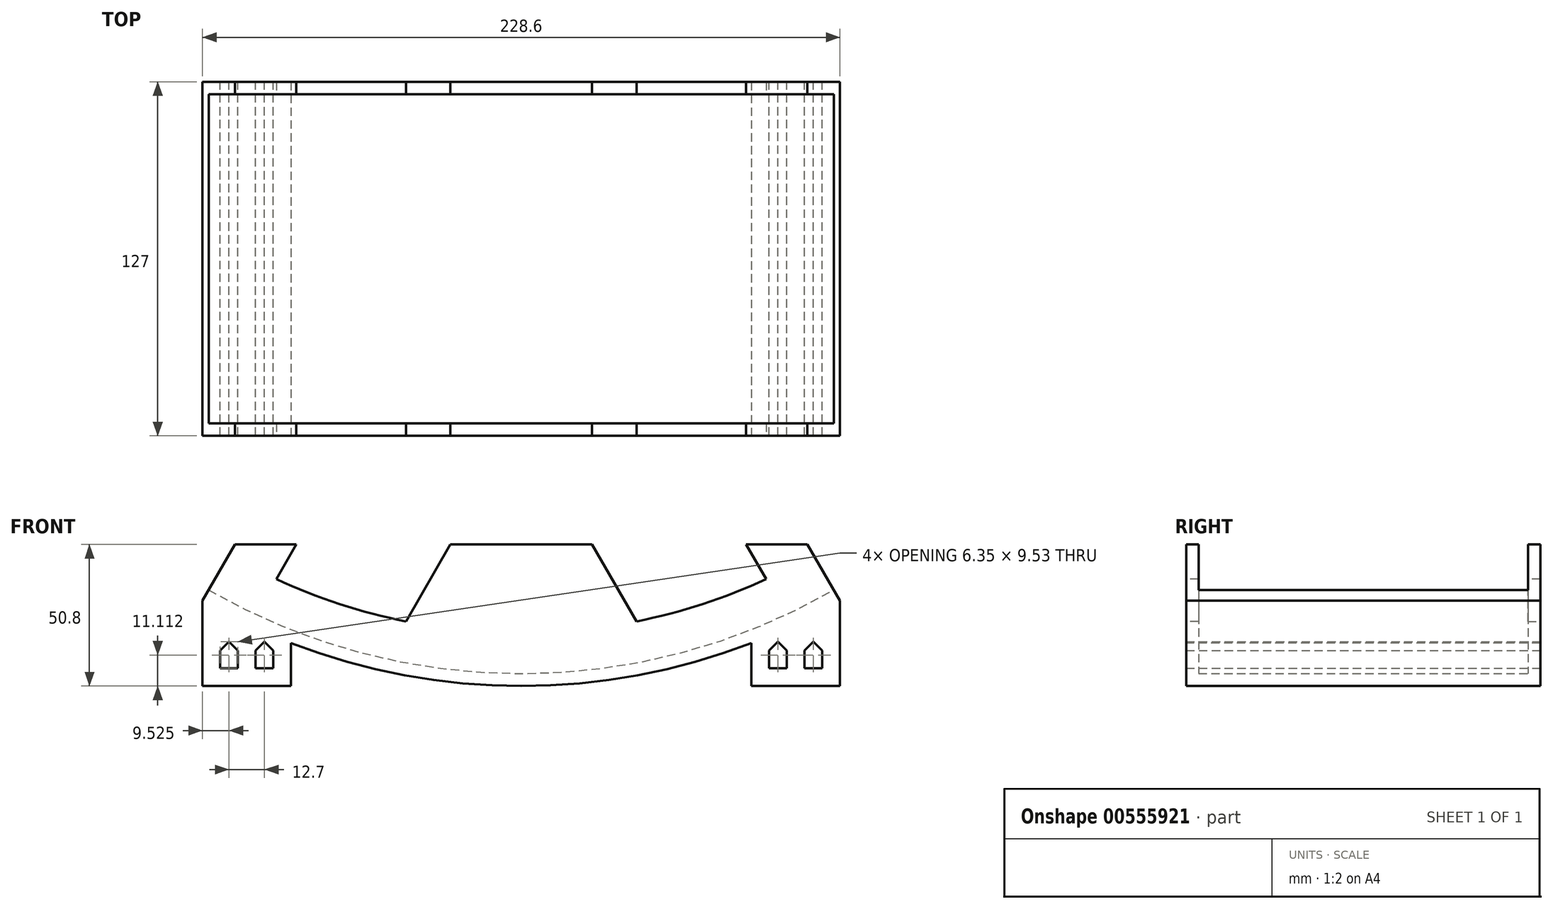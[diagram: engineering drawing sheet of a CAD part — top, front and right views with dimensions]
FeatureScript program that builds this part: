
annotation { "Feature Type Name" : "Feature", "Feature Type Description" : "" }
export const myFeature = defineFeature(function(context is Context, id is Id, definition is map)
    precondition{}
    {
        {
            var Q0;
            Q0=qCreatedBy(makeId("Front.planeOp"),FACE);
            var sketch = newSketch(context, id + "F0", { "sketchPlane" : qUnion([Q0])});
            skArc(sketch, "E0", {"start": v(-228.6, 0) * mm, "mid": v(0, -228.6) * mm, "end": v(228.6, 0) * mm});
            skLineSegment(sketch, "E1", {"start": v(-38.1, 0) * mm, "end": v(-228.6, 0) * mm});
            skLineSegment(sketch, "E2", {"start": v(38.1, 0) * mm, "end": v(228.6, 0) * mm});
            skLineSegment(sketch, "E3", {"start": v(-19.05, -33) * mm, "end": v(-114.3, -197.97) * mm});
            skLineSegment(sketch, "E4", {"start": v(19.05, -33) * mm, "end": v(114.3, -197.97) * mm});
            skArc(sketch, "E5", {"start": v(19.05, -33) * mm, "mid": v(0, 38.1) * mm, "end": v(-19.05, -33) * mm});
            skSolve(sketch);
        }
        {
            var Q0;
            {var subQ3=sQuery(id+"F0.wireOp",EDGE,"E3");Q0=makeQuery(id+"F0.imprint","IMPRINT",FACE,{"disambiguationData":[TD([[makeQuery(id+"F0.imprint","IMPRINT",EDGE,{"derivedFrom":subQ3}),1.0]])]});}
            extrude(context, id + "F1", {"entities" : qUnion([Q0]), "depth" : 127 * mm, "offsetDistance" : 25.4 * mm});
        }
        {
            var Q0;
            Q0=makeQuery(id+"F1.opExtrude","SWEPT_FACE",FACE,{"disambiguationData":[OSD([sQuery(id+"F0.wireOp",EDGE,"E5")])]});
            var Q1;
            Q1=makeQuery(id+"F1.opExtrude","SWEPT_FACE",FACE,{"disambiguationData":[OSD([sQuery(id+"F0.wireOp",EDGE,"E4")])]});
            var Q2;
            Q2=makeQuery(id+"F1.opExtrude","SWEPT_FACE",FACE,{"disambiguationData":[OSD([sQuery(id+"F0.wireOp",EDGE,"E3")])]});
            shell(context, id + "F2", {"entities" : qUnion([Q0, Q1, Q2]), "thickness" : 4.44 * mm});
        }
        {
            var Q0;
            Q0=makeQuery(id+"F1.opExtrude","CAP_FACE",FACE,{"disambiguationData":[OSD([sQuery(id+"F0.wireOp",EDGE,"E0"),sQuery(id+"F0.wireOp",EDGE,"E3"),sQuery(id+"F0.wireOp",EDGE,"E4"),sQuery(id+"F0.wireOp",EDGE,"E5")])],"isStart":false});
            var sketch = newSketch(context, id + "F3", { "sketchPlane" : qUnion([Q0])});
            skLineSegment(sketch, "E6.0", {"start": v(7.05, -50.3) * mm, "end": v(87.84, -190.25) * mm});
            skArc(sketch, "E6.1", {"start": v(-87.84, -190.25) * mm, "mid": v(-48.4, -203.88) * mm, "end": v(-7.05, -209.43) * mm});
            skCircle(sketch, "E7", {"center": v(0, 0) * mm, "radius": 9.53 * mm});
            skLineSegment(sketch, "E8", {"start": v(-7.05, -50.3) * mm, "end": v(-7.05, -125.9) * mm});
            skLineSegment(sketch, "E9", {"start": v(7.05, -50.3) * mm, "end": v(7.05, -125.9) * mm});
            skLineSegment(sketch, "E10", {"start": v(-87.84, -190.25) * mm, "end": v(-50.62, -125.78) * mm});
            skPoint(sketch, "E11.endSnap0", {"position": v(-66.67, -115.48) * mm});
            skLineSegment(sketch, "E12", {"start": v(-44.27, -114.78) * mm, "end": v(-14.9, -131.73) * mm});
            skLineSegment(sketch, "E13.trimOffspring", {"start": v(-7.05, -169.35) * mm, "end": v(-7.05, -209.43) * mm});
            skLineSegment(sketch, "E14.trimOffspring", {"start": v(-50.62, -125.78) * mm, "end": v(-87.84, -190.25) * mm});
            skArc(sketch, "E15.trimOffspring", {"start": v(7.05, -209.43) * mm, "mid": v(48.4, -203.88) * mm, "end": v(87.84, -190.25) * mm});
            skLineSegment(sketch, "E16", {"start": v(-7.05, -50.3) * mm, "end": v(0, -50.3) * mm, "construction": true});
            skLineSegment(sketch, "E17", {"start": v(0, -50.3) * mm, "end": v(0, -85.39) * mm, "construction": true});
            skLineSegment(sketch, "E18", {"start": v(-44.27, -114.78) * mm, "end": v(-7.05, -50.3) * mm});
            skLineSegment(sketch, "E19.MirrorCS", {"start": v(44.27, -114.78) * mm, "end": v(14.9, -131.73) * mm});
            skLineSegment(sketch, "E20.trimOffspring", {"start": v(7.05, -169.35) * mm, "end": v(7.05, -209.43) * mm});
            skArc(sketch, "E21", {"start": v(14.9, -131.73) * mm, "mid": v(11.36, -128.3) * mm, "end": v(7.05, -125.9) * mm});
            skPoint(sketch, "E22.orphan", {"position": v(7.05, -136.27) * mm});
            skPoint(sketch, "E23.orphan", {"position": v(7.05, -150.93) * mm});
            skPoint(sketch, "E24.orphan", {"position": v(-7.05, -150.93) * mm});
            skPoint(sketch, "E25.orphan", {"position": v(-7.05, -136.27) * mm});
            skLineSegment(sketch, "E26", {"start": v(50.62, -125.78) * mm, "end": v(7.05, -169.35) * mm, "construction": true});
            skLineSegment(sketch, "E27", {"start": v(50.62, -125.78) * mm, "end": v(7.05, -169.35) * mm});
            skLineSegment(sketch, "E28.MirrorCS", {"start": v(-50.62, -125.78) * mm, "end": v(-7.05, -169.35) * mm});
            skArc(sketch, "E29.trimOffspring", {"start": v(-7.05, -125.9) * mm, "mid": v(-11.36, -128.3) * mm, "end": v(-14.9, -131.73) * mm});
            skSolve(sketch);
        }
        {
            var Q0;
            Q0=makeQuery(id+"F3.imprint","IMPRINT",FACE,{"disambiguationData":[TD([[makeQuery(id+"F3.imprint","IMPRINT",EDGE,{"derivedFrom":sQuery(id+"F3.wireOp",EDGE,"E6.1")}),1.0]])]});
            var Q1;
            {var subQ2=sQuery(id+"F3.wireOp",EDGE,"E15.trimOffspring");Q1=makeQuery(id+"F3.imprint","IMPRINT",FACE,{"disambiguationData":[TD([[makeQuery(id+"F3.imprint","IMPRINT",EDGE,{"derivedFrom":subQ2}),1.0]])]});}
            var Q2;
            {var subQ0=sQuery(id+"F3.wireOp",EDGE,"E9");Q2=makeQuery(id+"F3.imprint","IMPRINT",FACE,{"disambiguationData":[TD([[makeQuery(id+"F3.imprint","IMPRINT",EDGE,{"derivedFrom":subQ0}),1.0]])]});}
            var Q3;
            {var subQ0=sQuery(id+"F3.wireOp",EDGE,"E8");Q3=makeQuery(id+"F3.imprint","IMPRINT",FACE,{"disambiguationData":[TD([[makeQuery(id+"F3.imprint","IMPRINT",EDGE,{"derivedFrom":subQ0}),-1.0]])]});}
            var Q4;
            Q4=makeQuery(id+"F3.imprint","IMPRINT",FACE,{"disambiguationData":[TD([[makeQuery(id+"F3.imprint","IMPRINT",EDGE,{"derivedFrom":sQuery(id+"F3.wireOp",EDGE,"E7")}),1.0]])]});
            var Q5;
            Q5=makeQuery(id+"F1.opExtrude","CAP_FACE",FACE,{"disambiguationData":[OSD([sQuery(id+"F0.wireOp",EDGE,"E0"),sQuery(id+"F0.wireOp",EDGE,"E3"),sQuery(id+"F0.wireOp",EDGE,"E4"),sQuery(id+"F0.wireOp",EDGE,"E5")])],"isStart":true});
            extrude(context, id + "F4", {"entities" : qUnion([Q0, Q1, Q2, Q3, Q4]), "operationType" : NewBodyOperationType.REMOVE, "endBound" : BoundingType.UP_TO_SURFACE, "oppositeDirection" : true, "depth" : 25.4 * mm, "endBoundEntityFace" : qUnion([Q5]), "offsetDistance" : 25.4 * mm});
        }
        {
            var Q0;
            Q0=qCreatedBy(makeId("Front.planeOp"),FACE);
            var sketch = newSketch(context, id + "F5", { "sketchPlane" : qUnion([Q0])});
            skLineSegment(sketch, "E30", {"start": v(0, -228.6) * mm, "end": v(114.3, -228.6) * mm});
            skLineSegment(sketch, "E31", {"start": v(0, -228.6) * mm, "end": v(-114.3, -228.6) * mm});
            skLineSegment(sketch, "E32", {"start": v(114.3, -197.97) * mm, "end": v(114.3, -228.6) * mm});
            skLineSegment(sketch, "E33", {"start": v(-114.3, -197.97) * mm, "end": v(-114.3, -228.6) * mm});
            skPoint(sketch, "E34.orphan", {"position": v(-122.47, -228.6) * mm});
            skArc(sketch, "E35.0", {"start": v(-114.3, -197.97) * mm, "mid": v(0, -228.6) * mm, "end": v(114.3, -197.97) * mm});
            skLineSegment(sketch, "E36", {"start": v(114.3, -228.6) * mm, "end": v(107.95, -228.6) * mm, "construction": true});
            skLineSegment(sketch, "E37", {"start": v(107.95, -228.6) * mm, "end": v(107.95, -222.25) * mm, "construction": true});
            skLineSegment(sketch, "E38.bottom", {"start": v(107.95, -222.25) * mm, "end": v(101.6, -222.25) * mm});
            skLineSegment(sketch, "E38.left", {"start": v(107.95, -222.25) * mm, "end": v(107.95, -215.9) * mm});
            skLineSegment(sketch, "E38.right", {"start": v(88.9, -222.25) * mm, "end": v(88.9, -215.9) * mm});
            skLineSegment(sketch, "E39", {"start": v(101.6, -222.25) * mm, "end": v(101.6, -215.9) * mm});
            skLineSegment(sketch, "E40", {"start": v(95.25, -222.25) * mm, "end": v(95.25, -215.9) * mm});
            skLineSegment(sketch, "E41.trimOffspring", {"start": v(95.25, -222.25) * mm, "end": v(88.9, -222.25) * mm});
            skLineSegment(sketch, "E42", {"start": v(104.78, -215.9) * mm, "end": v(104.78, -212.72) * mm, "construction": true});
            skLineSegment(sketch, "E43", {"start": v(92.08, -215.9) * mm, "end": v(92.08, -212.72) * mm, "construction": true});
            skLineSegment(sketch, "E44", {"start": v(107.95, -215.9) * mm, "end": v(104.78, -212.72) * mm});
            skLineSegment(sketch, "E45", {"start": v(101.6, -215.9) * mm, "end": v(104.78, -212.72) * mm});
            skLineSegment(sketch, "E46", {"start": v(95.25, -215.9) * mm, "end": v(92.08, -212.72) * mm});
            skLineSegment(sketch, "E47", {"start": v(88.9, -215.9) * mm, "end": v(92.08, -212.72) * mm});
            skLineSegment(sketch, "E48.MirrorCS", {"start": v(-104.78, -215.9) * mm, "end": v(-104.78, -212.72) * mm, "construction": true});
            skLineSegment(sketch, "E49.MirrorCS", {"start": v(-92.08, -215.9) * mm, "end": v(-92.08, -212.72) * mm, "construction": true});
            skLineSegment(sketch, "E50.MirrorCS", {"start": v(-101.6, -215.9) * mm, "end": v(-104.78, -212.72) * mm});
            skLineSegment(sketch, "E51.MirrorCS", {"start": v(-88.9, -215.9) * mm, "end": v(-92.08, -212.72) * mm});
            skLineSegment(sketch, "E52.MirrorCS", {"start": v(-107.95, -215.9) * mm, "end": v(-104.78, -212.72) * mm});
            skLineSegment(sketch, "E53.MirrorCS", {"start": v(-95.25, -222.25) * mm, "end": v(-95.25, -215.9) * mm});
            skLineSegment(sketch, "E54.MirrorCS", {"start": v(-101.6, -222.25) * mm, "end": v(-101.6, -215.9) * mm});
            skLineSegment(sketch, "E55.MirrorCS", {"start": v(-107.95, -222.25) * mm, "end": v(-107.95, -215.9) * mm});
            skLineSegment(sketch, "E56.MirrorCS", {"start": v(-107.95, -222.25) * mm, "end": v(-101.6, -222.25) * mm});
            skLineSegment(sketch, "E57.MirrorCS", {"start": v(-88.9, -222.25) * mm, "end": v(-88.9, -215.9) * mm});
            skLineSegment(sketch, "E58.MirrorCS", {"start": v(-95.25, -215.9) * mm, "end": v(-92.08, -212.72) * mm});
            skLineSegment(sketch, "E59.MirrorCS", {"start": v(-95.25, -222.25) * mm, "end": v(-88.9, -222.25) * mm});
            skSolve(sketch);
        }
        {
            var Q0;
            {var subQ2=sQuery(id+"F5.wireOp",EDGE,"E30");Q0=makeQuery(id+"F5.imprint","IMPRINT",FACE,{"disambiguationData":[TD([[makeQuery(id+"F5.imprint","IMPRINT",EDGE,{"derivedFrom":subQ2}),1.0]])]});}
            var Q1;
            {var subQ2=sQuery(id+"F5.wireOp",EDGE,"E31");Q1=makeQuery(id+"F5.imprint","IMPRINT",FACE,{"disambiguationData":[TD([[makeQuery(id+"F5.imprint","IMPRINT",EDGE,{"derivedFrom":subQ2}),-1.0]])]});}
            var Q2;
            Q2=makeQuery(id+"F1.opExtrude","CAP_FACE",FACE,{"disambiguationData":[OSD([sQuery(id+"F0.wireOp",EDGE,"E0"),sQuery(id+"F0.wireOp",EDGE,"E3"),sQuery(id+"F0.wireOp",EDGE,"E4"),sQuery(id+"F0.wireOp",EDGE,"E5")])],"isStart":false});
            extrude(context, id + "F6", {"entities" : qUnion([Q0, Q1]), "operationType" : NewBodyOperationType.ADD, "endBound" : BoundingType.UP_TO_SURFACE, "depth" : 25.4 * mm, "endBoundEntityFace" : qUnion([Q2]), "offsetDistance" : 25.4 * mm});
        }
        {
            var Q0;
            Q0=qCreatedBy(makeId("Front.planeOp"),FACE);
            var sketch = newSketch(context, id + "F7", { "sketchPlane" : qUnion([Q0])});
            skLineSegment(sketch, "E60", {"start": v(0, 0) * mm, "end": v(0, -177.8) * mm, "construction": true});
            skLineSegment(sketch, "E61", {"start": v(0, -177.8) * mm, "end": v(122.5, -177.8) * mm});
            skLineSegment(sketch, "E62", {"start": v(122.5, -177.8) * mm, "end": v(122.5, 99.95) * mm});
            skLineSegment(sketch, "E63", {"start": v(0, -177.8) * mm, "end": v(-155.13, -177.8) * mm});
            skLineSegment(sketch, "E64", {"start": v(-155.13, -177.8) * mm, "end": v(-155.13, 97.68) * mm});
            skLineSegment(sketch, "E65", {"start": v(-155.13, 97.68) * mm, "end": v(122.5, 99.95) * mm});
            skSolve(sketch);
        }
        {
            var Q0;
            Q0=makeQuery(id+"F7.imprint","IMPRINT",FACE,{"disambiguationData":[TD([[makeQuery(id+"F7.imprint","IMPRINT",EDGE,{"derivedFrom":sQuery(id+"F7.wireOp",EDGE,"E61")}),1.0]])]});
            extrude(context, id + "F8", {"entities" : qUnion([Q0]), "operationType" : NewBodyOperationType.REMOVE, "depth" : 154.94 * mm, "offsetDistance" : 25.4 * mm});
        }
        {
            var Q0;
            {var subQ0=sQuery(id+"F5.wireOp",EDGE,"E35.0");Q0=makeQuery(id+"F6.boolean.opBoolean","MERGE",FACE,{"derivedFrom":[makeQuery(id+"F1.opExtrude","CAP_FACE",FACE,{"disambiguationData":[OSD([sQuery(id+"F0.wireOp",EDGE,"E0"),sQuery(id+"F0.wireOp",EDGE,"E3"),sQuery(id+"F0.wireOp",EDGE,"E4"),sQuery(id+"F0.wireOp",EDGE,"E5")])],"isStart":true}),makeQuery(id+"F6.opExtrude","CAP_FACE",FACE,{"disambiguationData":[OSD([sQuery(id+"F5.wireOp",EDGE,"E30"),sQuery(id+"F5.wireOp",EDGE,"E32"),subQ0,sQuery(id+"F5.wireOp",EDGE,"E38.bottom"),sQuery(id+"F5.wireOp",EDGE,"E38.left"),sQuery(id+"F5.wireOp",EDGE,"E38.right"),sQuery(id+"F5.wireOp",EDGE,"E39"),sQuery(id+"F5.wireOp",EDGE,"E40"),sQuery(id+"F5.wireOp",EDGE,"E41.trimOffspring"),sQuery(id+"F5.wireOp",EDGE,"E44"),sQuery(id+"F5.wireOp",EDGE,"E45"),sQuery(id+"F5.wireOp",EDGE,"E46"),sQuery(id+"F5.wireOp",EDGE,"E47")])],"isStart":true}),makeQuery(id+"F6.opExtrude","CAP_FACE",FACE,{"disambiguationData":[OSD([sQuery(id+"F5.wireOp",EDGE,"E31"),sQuery(id+"F5.wireOp",EDGE,"E33"),subQ0,sQuery(id+"F5.wireOp",EDGE,"E50.MirrorCS"),sQuery(id+"F5.wireOp",EDGE,"E51.MirrorCS"),sQuery(id+"F5.wireOp",EDGE,"E52.MirrorCS"),sQuery(id+"F5.wireOp",EDGE,"E53.MirrorCS"),sQuery(id+"F5.wireOp",EDGE,"E54.MirrorCS"),sQuery(id+"F5.wireOp",EDGE,"E55.MirrorCS"),sQuery(id+"F5.wireOp",EDGE,"E56.MirrorCS"),sQuery(id+"F5.wireOp",EDGE,"E57.MirrorCS"),sQuery(id+"F5.wireOp",EDGE,"E58.MirrorCS"),sQuery(id+"F5.wireOp",EDGE,"E59.MirrorCS")])],"isStart":true})]});}
            var sketch = newSketch(context, id + "F9", { "sketchPlane" : qUnion([Q0])});
            skArc(sketch, "E66.0", {"start": v(-87.84, -190.25) * mm, "mid": v(-48.4, -203.88) * mm, "end": v(-7.05, -209.43) * mm});
            skLineSegment(sketch, "E67.0", {"start": v(-7.05, -209.43) * mm, "end": v(-7.05, -177.8) * mm});
            skLineSegment(sketch, "E68", {"start": v(0, -177.8) * mm, "end": v(25.4, -177.8) * mm});
            skLineSegment(sketch, "E69", {"start": v(0, -177.8) * mm, "end": v(-25.4, -177.8) * mm});
            skLineSegment(sketch, "E70", {"start": v(-25.4, -177.8) * mm, "end": v(-41.35, -205.43) * mm});
            skLineSegment(sketch, "E71", {"start": v(25.4, -177.8) * mm, "end": v(41.35, -205.43) * mm});
            skLineSegment(sketch, "E72.0", {"start": v(7.05, -209.43) * mm, "end": v(7.05, -177.8) * mm});
            skArc(sketch, "E73.0", {"start": v(7.05, -209.43) * mm, "mid": v(48.4, -203.88) * mm, "end": v(87.84, -190.25) * mm});
            skSolve(sketch);
        }
        {
            var Q0;
            {var subQ0=sQuery(id+"F9.wireOp",EDGE,"E67.0");Q0=makeQuery(id+"F9.imprint","IMPRINT",FACE,{"disambiguationData":[TD([[makeQuery(id+"F9.imprint","IMPRINT",EDGE,{"derivedFrom":subQ0}),1.0]])]});}
            var Q1;
            {var subQ2=sQuery(id+"F9.wireOp",EDGE,"E71");Q1=makeQuery(id+"F9.imprint","IMPRINT",FACE,{"disambiguationData":[TD([[makeQuery(id+"F9.imprint","IMPRINT",EDGE,{"derivedFrom":subQ2}),-1.0]])]});}
            var Q2;
            {var subQ0=sQuery(id+"F0.wireOp",EDGE,"E5");var subQ1=sQuery(id+"F0.wireOp",EDGE,"E4");var subQ2=sQuery(id+"F0.wireOp",EDGE,"E3");var subQ3=sQuery(id+"F0.wireOp",EDGE,"E0");Q2=makeQuery(id+"F2.opShell","OFFSET_FACE",FACE,{"disambiguationData":[OSD([subQ3,subQ2,subQ1,subQ0]),TDD([makeQuery(id+"F1.opExtrude","CAP_FACE",FACE,{"disambiguationData":[OSD([subQ3,subQ2,subQ1,subQ0])],"isStart":true})])]});}
            extrude(context, id + "F10", {"entities" : qUnion([Q0, Q1]), "operationType" : NewBodyOperationType.ADD, "endBound" : BoundingType.UP_TO_SURFACE, "oppositeDirection" : true, "depth" : 25.4 * mm, "endBoundEntityFace" : qUnion([Q2]), "offsetDistance" : 25.4 * mm});
        }
        {
            var Q0;
            Q0=qCreatedBy(makeId("Front.planeOp"),FACE);
            var Q1;
            {var subQ0=sQuery(id+"F5.wireOp",EDGE,"E35.0");Q1=makeQuery(id+"F6.boolean.opBoolean","MERGE",FACE,{"derivedFrom":[makeQuery(id+"F1.opExtrude","CAP_FACE",FACE,{"disambiguationData":[OSD([sQuery(id+"F0.wireOp",EDGE,"E0"),sQuery(id+"F0.wireOp",EDGE,"E3"),sQuery(id+"F0.wireOp",EDGE,"E4"),sQuery(id+"F0.wireOp",EDGE,"E5")])],"isStart":false}),makeQuery(id+"F6.opExtrude","CAP_FACE",FACE,{"disambiguationData":[OSD([sQuery(id+"F5.wireOp",EDGE,"E30"),sQuery(id+"F5.wireOp",EDGE,"E32"),subQ0,sQuery(id+"F5.wireOp",EDGE,"E38.bottom"),sQuery(id+"F5.wireOp",EDGE,"E38.left"),sQuery(id+"F5.wireOp",EDGE,"E38.right"),sQuery(id+"F5.wireOp",EDGE,"E39"),sQuery(id+"F5.wireOp",EDGE,"E40"),sQuery(id+"F5.wireOp",EDGE,"E41.trimOffspring"),sQuery(id+"F5.wireOp",EDGE,"E44"),sQuery(id+"F5.wireOp",EDGE,"E45"),sQuery(id+"F5.wireOp",EDGE,"E46"),sQuery(id+"F5.wireOp",EDGE,"E47")])],"isStart":false}),makeQuery(id+"F6.opExtrude","CAP_FACE",FACE,{"disambiguationData":[OSD([sQuery(id+"F5.wireOp",EDGE,"E31"),sQuery(id+"F5.wireOp",EDGE,"E33"),subQ0,sQuery(id+"F5.wireOp",EDGE,"E50.MirrorCS"),sQuery(id+"F5.wireOp",EDGE,"E51.MirrorCS"),sQuery(id+"F5.wireOp",EDGE,"E52.MirrorCS"),sQuery(id+"F5.wireOp",EDGE,"E53.MirrorCS"),sQuery(id+"F5.wireOp",EDGE,"E54.MirrorCS"),sQuery(id+"F5.wireOp",EDGE,"E55.MirrorCS"),sQuery(id+"F5.wireOp",EDGE,"E56.MirrorCS"),sQuery(id+"F5.wireOp",EDGE,"E57.MirrorCS"),sQuery(id+"F5.wireOp",EDGE,"E58.MirrorCS"),sQuery(id+"F5.wireOp",EDGE,"E59.MirrorCS")])],"isStart":false})]});}
            cPlane(context, id + "F11", {"entities" : qUnion([Q0, Q1]), "cplaneType" : CPlaneType.MID_PLANE, "offset" : 25.4 * mm, "width" : 152.4 * mm, "height" : 152.4 * mm});
        }
        {
            var Q0;
            Q0=makeQuery(id+"F1.opExtrude","SWEPT_BODY",BODY,{"disambiguationData":[OSD([sQuery(id+"F0.wireOp",EDGE,"E0"),sQuery(id+"F0.wireOp",EDGE,"E3"),sQuery(id+"F0.wireOp",EDGE,"E4"),sQuery(id+"F0.wireOp",EDGE,"E5")])]});
            var Q1;
            Q1=qCreatedBy(id+"F11.planeOp",FACE);
            mirror(context, id + "F12", {"operationType" : NewBodyOperationType.ADD, "entities" : qUnion([Q0]), "mirrorPlane" : qUnion([Q1])});
        }
        {
            var Q0;
            {var subQ0=sQuery(id+"F5.wireOp",EDGE,"E59.MirrorCS");var subQ1=sQuery(id+"F5.wireOp",EDGE,"E58.MirrorCS");var subQ2=sQuery(id+"F5.wireOp",EDGE,"E57.MirrorCS");var subQ3=sQuery(id+"F5.wireOp",EDGE,"E56.MirrorCS");var subQ4=sQuery(id+"F5.wireOp",EDGE,"E55.MirrorCS");var subQ5=sQuery(id+"F5.wireOp",EDGE,"E54.MirrorCS");var subQ6=sQuery(id+"F5.wireOp",EDGE,"E53.MirrorCS");var subQ7=sQuery(id+"F5.wireOp",EDGE,"E52.MirrorCS");var subQ8=sQuery(id+"F5.wireOp",EDGE,"E51.MirrorCS");var subQ9=sQuery(id+"F5.wireOp",EDGE,"E50.MirrorCS");var subQ10=sQuery(id+"F5.wireOp",EDGE,"E35.0");var subQ11=sQuery(id+"F5.wireOp",EDGE,"E33");var subQ12=sQuery(id+"F5.wireOp",EDGE,"E31");var subQ13=sQuery(id+"F5.wireOp",EDGE,"E47");var subQ14=sQuery(id+"F5.wireOp",EDGE,"E46");var subQ15=sQuery(id+"F5.wireOp",EDGE,"E45");var subQ16=sQuery(id+"F5.wireOp",EDGE,"E44");var subQ17=sQuery(id+"F5.wireOp",EDGE,"E41.trimOffspring");var subQ18=sQuery(id+"F5.wireOp",EDGE,"E40");var subQ19=sQuery(id+"F5.wireOp",EDGE,"E39");var subQ20=sQuery(id+"F5.wireOp",EDGE,"E38.right");var subQ21=sQuery(id+"F5.wireOp",EDGE,"E38.left");var subQ22=sQuery(id+"F5.wireOp",EDGE,"E38.bottom");var subQ23=sQuery(id+"F5.wireOp",EDGE,"E32");var subQ24=sQuery(id+"F5.wireOp",EDGE,"E30");var subQ25=sQuery(id+"F0.wireOp",EDGE,"E5");var subQ26=sQuery(id+"F0.wireOp",EDGE,"E4");var subQ27=sQuery(id+"F0.wireOp",EDGE,"E3");var subQ28=sQuery(id+"F0.wireOp",EDGE,"E0");Q0=makeQuery(id+"F12.boolean.opBoolean","MERGE",FACE,{"derivedFrom":[makeQuery(id+"F6.boolean.opBoolean","MERGE",FACE,{"derivedFrom":[makeQuery(id+"F1.opExtrude","CAP_FACE",FACE,{"disambiguationData":[OSD([subQ28,subQ27,subQ26,subQ25])],"isStart":false}),makeQuery(id+"F6.opExtrude","CAP_FACE",FACE,{"disambiguationData":[OSD([subQ24,subQ23,subQ10,subQ22,subQ21,subQ20,subQ19,subQ18,subQ17,subQ16,subQ15,subQ14,subQ13])],"isStart":false}),makeQuery(id+"F6.opExtrude","CAP_FACE",FACE,{"disambiguationData":[OSD([subQ12,subQ11,subQ10,subQ9,subQ8,subQ7,subQ6,subQ5,subQ4,subQ3,subQ2,subQ1,subQ0])],"isStart":false})]}),makeQuery(id+"F12.opPattern","COPY",FACE,{"derivedFrom":makeQuery(id+"F10.boolean.opBoolean","MERGE",FACE,{"derivedFrom":[makeQuery(id+"F6.boolean.opBoolean","MERGE",FACE,{"derivedFrom":[makeQuery(id+"F1.opExtrude","CAP_FACE",FACE,{"disambiguationData":[OSD([subQ28,subQ27,subQ26,subQ25])],"isStart":true}),makeQuery(id+"F6.opExtrude","CAP_FACE",FACE,{"disambiguationData":[OSD([subQ24,subQ23,subQ10,subQ22,subQ21,subQ20,subQ19,subQ18,subQ17,subQ16,subQ15,subQ14,subQ13])],"isStart":true}),makeQuery(id+"F6.opExtrude","CAP_FACE",FACE,{"disambiguationData":[OSD([subQ12,subQ11,subQ10,subQ9,subQ8,subQ7,subQ6,subQ5,subQ4,subQ3,subQ2,subQ1,subQ0])],"isStart":true})]}),makeQuery(id+"F10.opExtrude","CAP_FACE",FACE,{"disambiguationData":[OSD([sQuery(id+"F9.wireOp",EDGE,"E66.0"),sQuery(id+"F9.wireOp",EDGE,"E67.0"),sQuery(id+"F9.wireOp",EDGE,"E69"),sQuery(id+"F9.wireOp",EDGE,"E70")])],"isStart":true}),makeQuery(id+"F10.opExtrude","CAP_FACE",FACE,{"disambiguationData":[OSD([sQuery(id+"F9.wireOp",EDGE,"E68"),sQuery(id+"F9.wireOp",EDGE,"E71"),sQuery(id+"F9.wireOp",EDGE,"E72.0"),sQuery(id+"F9.wireOp",EDGE,"E73.0")])],"isStart":true})]}),"instanceName":"1"})]});}
            var sketch = newSketch(context, id + "F13", { "sketchPlane" : qUnion([Q0])});
            skArc(sketch, "E74", {"start": v(-114.3, -197.97) * mm, "mid": v(0, -228.6) * mm, "end": v(114.3, -197.97) * mm});
            skLineSegment(sketch, "E75.0", {"start": v(114.3, -228.6) * mm, "end": v(-114.3, -228.6) * mm});
            skLineSegment(sketch, "E76", {"start": v(-82.55, -228.6) * mm, "end": v(-82.55, -213.17) * mm});
            skLineSegment(sketch, "E77.MirrorCS", {"start": v(82.55, -228.6) * mm, "end": v(82.55, -213.17) * mm});
            skArc(sketch, "E78.MirrorCS", {"start": v(114.3, -197.97) * mm, "mid": v(0, -228.6) * mm, "end": v(-114.3, -197.97) * mm});
            skLineSegment(sketch, "E79.MirrorCS", {"start": v(-114.3, -228.6) * mm, "end": v(114.3, -228.6) * mm});
            skSolve(sketch);
        }
        {
            var Q0;
            {var subQ0=sQuery(id+"F13.wireOp",EDGE,"E76");Q0=makeQuery(id+"F13.imprint","IMPRINT",FACE,{"disambiguationData":[TD([[makeQuery(id+"F13.imprint","IMPRINT",EDGE,{"derivedFrom":subQ0}),-1.0]])]});}
            var Q1;
            {var subQ0=sQuery(id+"F13.wireOp",EDGE,"E77.MirrorCS");Q1=makeQuery(id+"F13.imprint","IMPRINT",FACE,{"disambiguationData":[TD([[makeQuery(id+"F13.imprint","IMPRINT",EDGE,{"derivedFrom":subQ0}),1.0]])]});}
            var Q2;
            {var subQ0=sQuery(id+"F5.wireOp",EDGE,"E35.0");Q2=makeQuery(id+"F10.boolean.opBoolean","MERGE",FACE,{"derivedFrom":[makeQuery(id+"F6.boolean.opBoolean","MERGE",FACE,{"derivedFrom":[makeQuery(id+"F1.opExtrude","CAP_FACE",FACE,{"disambiguationData":[OSD([sQuery(id+"F0.wireOp",EDGE,"E0"),sQuery(id+"F0.wireOp",EDGE,"E3"),sQuery(id+"F0.wireOp",EDGE,"E4"),sQuery(id+"F0.wireOp",EDGE,"E5")])],"isStart":true}),makeQuery(id+"F6.opExtrude","CAP_FACE",FACE,{"disambiguationData":[OSD([sQuery(id+"F5.wireOp",EDGE,"E30"),sQuery(id+"F5.wireOp",EDGE,"E32"),subQ0,sQuery(id+"F5.wireOp",EDGE,"E38.bottom"),sQuery(id+"F5.wireOp",EDGE,"E38.left"),sQuery(id+"F5.wireOp",EDGE,"E38.right"),sQuery(id+"F5.wireOp",EDGE,"E39"),sQuery(id+"F5.wireOp",EDGE,"E40"),sQuery(id+"F5.wireOp",EDGE,"E41.trimOffspring"),sQuery(id+"F5.wireOp",EDGE,"E44"),sQuery(id+"F5.wireOp",EDGE,"E45"),sQuery(id+"F5.wireOp",EDGE,"E46"),sQuery(id+"F5.wireOp",EDGE,"E47")])],"isStart":true}),makeQuery(id+"F6.opExtrude","CAP_FACE",FACE,{"disambiguationData":[OSD([sQuery(id+"F5.wireOp",EDGE,"E31"),sQuery(id+"F5.wireOp",EDGE,"E33"),subQ0,sQuery(id+"F5.wireOp",EDGE,"E50.MirrorCS"),sQuery(id+"F5.wireOp",EDGE,"E51.MirrorCS"),sQuery(id+"F5.wireOp",EDGE,"E52.MirrorCS"),sQuery(id+"F5.wireOp",EDGE,"E53.MirrorCS"),sQuery(id+"F5.wireOp",EDGE,"E54.MirrorCS"),sQuery(id+"F5.wireOp",EDGE,"E55.MirrorCS"),sQuery(id+"F5.wireOp",EDGE,"E56.MirrorCS"),sQuery(id+"F5.wireOp",EDGE,"E57.MirrorCS"),sQuery(id+"F5.wireOp",EDGE,"E58.MirrorCS"),sQuery(id+"F5.wireOp",EDGE,"E59.MirrorCS")])],"isStart":true})]}),makeQuery(id+"F10.opExtrude","CAP_FACE",FACE,{"disambiguationData":[OSD([sQuery(id+"F9.wireOp",EDGE,"E66.0"),sQuery(id+"F9.wireOp",EDGE,"E67.0"),sQuery(id+"F9.wireOp",EDGE,"E69"),sQuery(id+"F9.wireOp",EDGE,"E70")])],"isStart":true}),makeQuery(id+"F10.opExtrude","CAP_FACE",FACE,{"disambiguationData":[OSD([sQuery(id+"F9.wireOp",EDGE,"E68"),sQuery(id+"F9.wireOp",EDGE,"E71"),sQuery(id+"F9.wireOp",EDGE,"E72.0"),sQuery(id+"F9.wireOp",EDGE,"E73.0")])],"isStart":true})]});}
            extrude(context, id + "F14", {"entities" : qUnion([Q0, Q1]), "operationType" : NewBodyOperationType.REMOVE, "endBound" : BoundingType.UP_TO_SURFACE, "oppositeDirection" : true, "depth" : 25.4 * mm, "endBoundEntityFace" : qUnion([Q2]), "offsetDistance" : 25.4 * mm});
        }
    });
